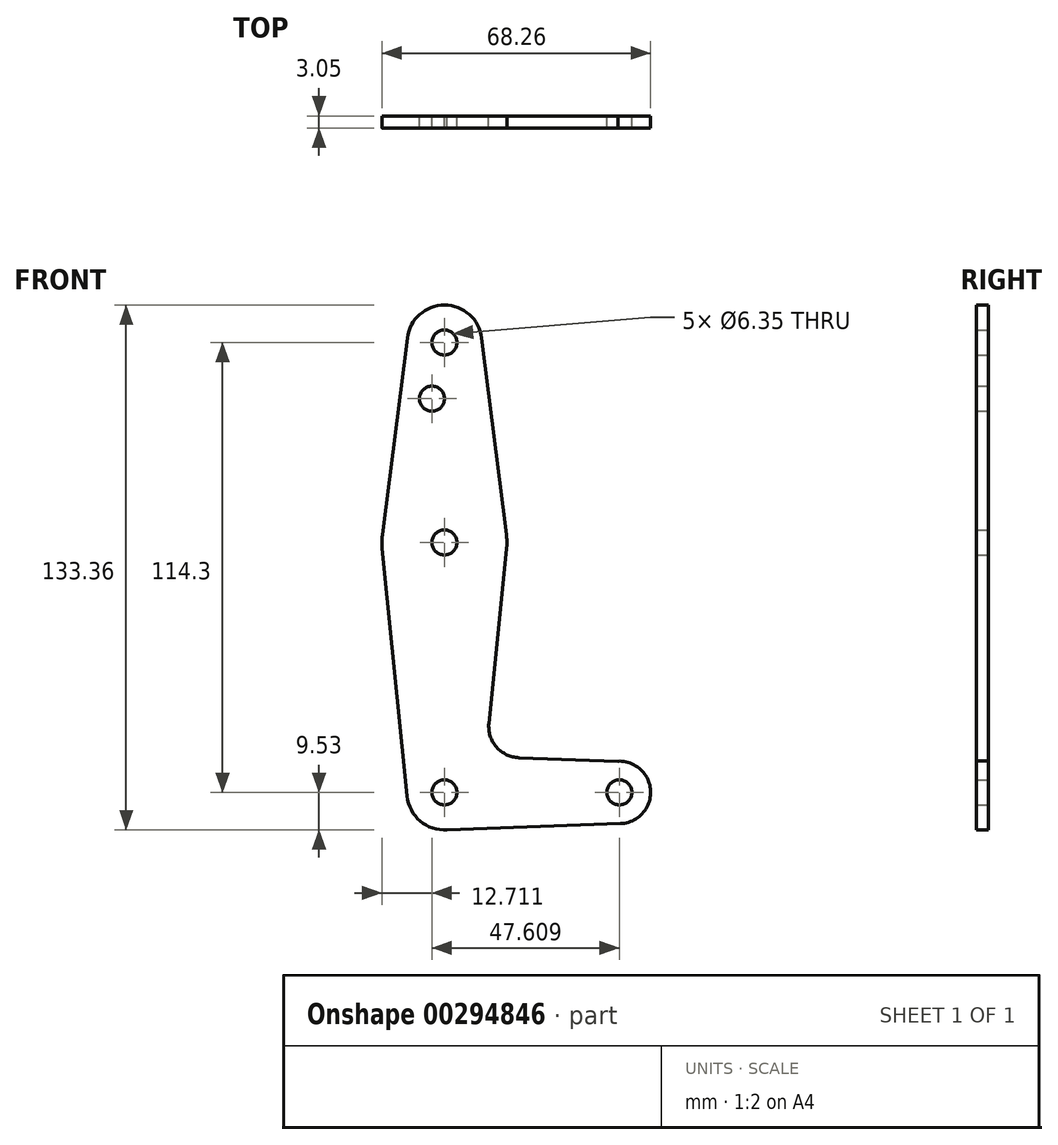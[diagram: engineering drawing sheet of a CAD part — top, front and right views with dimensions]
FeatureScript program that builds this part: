
annotation { "Feature Type Name" : "Feature", "Feature Type Description" : "" }
export const myFeature = defineFeature(function(context is Context, id is Id, definition is map)
    precondition{}
    {
        {
            var Q0;
            Q0=qCreatedBy(makeId("Front.planeOp"),FACE);
            var sketch = newSketch(context, id + "F0", { "sketchPlane" : qUnion([Q0])});
            skArc(sketch, "E0", {"start": v(0, 9.52) * mm, "mid": v(-0.34, -9.52) * mm, "end": v(0.68, 9.5) * mm});
            skCircle(sketch, "E1", {"center": v(0, 63.5) * mm, "radius": 15.88 * mm});
            skCircle(sketch, "E2", {"center": v(0.02, 114.3) * mm, "radius": 9.53 * mm});
            skCircle(sketch, "E3", {"center": v(44.45, 0) * mm, "radius": 7.94 * mm});
            skLineSegment(sketch, "E4", {"start": v(-9.43, 115.5) * mm, "end": v(-15.75, 65.5) * mm});
            skLineSegment(sketch, "E5", {"start": v(9.47, 115.49) * mm, "end": v(15.75, 65.5) * mm});
            skLineSegment(sketch, "E6", {"start": v(0, 9.52) * mm, "end": v(0.68, 9.5) * mm});
            skLineSegment(sketch, "E7", {"start": v(44.45, 0) * mm, "end": v(0, 0) * mm, "construction": true});
            skLineSegment(sketch, "E8", {"start": v(0, 63.5) * mm, "end": v(0, 0) * mm, "construction": true});
            skLineSegment(sketch, "E9", {"start": v(0.02, 114.3) * mm, "end": v(0, 63.5) * mm, "construction": true});
            skPoint(sketch, "E10.newPointB", {"position": v(9.52, 0) * mm});
            skCircle(sketch, "E11", {"center": v(0, 114.3) * mm, "radius": 3.18 * mm});
            skCircle(sketch, "E12", {"center": v(-3.16, 100.03) * mm, "radius": 3.18 * mm});
            skCircle(sketch, "E13", {"center": v(0, 63.5) * mm, "radius": 3.18 * mm});
            skCircle(sketch, "E14", {"center": v(0, 0) * mm, "radius": 3.18 * mm});
            skCircle(sketch, "E15", {"center": v(44.45, 0) * mm, "radius": 3.18 * mm});
            skLineSegment(sketch, "E16", {"start": v(-15.8, 61.91) * mm, "end": v(-9.48, -0.95) * mm});
            skLineSegment(sketch, "E17", {"start": v(44.1, 7.93) * mm, "end": v(18.93, 8.81) * mm});
            skLineSegment(sketch, "E18", {"start": v(0, -9.52) * mm, "end": v(44.73, -7.93) * mm});
            skLineSegment(sketch, "E19", {"start": v(15.8, 61.97) * mm, "end": v(11.3, 17.56) * mm});
            skPoint(sketch, "E20.newPointB", {"position": v(-0.68, 9.5) * mm});
            skArc(sketch, "E20.filletArc", {"start": v(11.3, 17.56) * mm, "mid": v(13.22, 11.53) * mm, "end": v(18.93, 8.81) * mm});
            skSolve(sketch);
        }
        {
            var Q0;
            Q0 = qSketchRegion(id + "F0", true);
            extrude(context, id + "F1", {"entities" : qUnion([Q0]), "depth" : 3.05 * mm});
        }
    });
